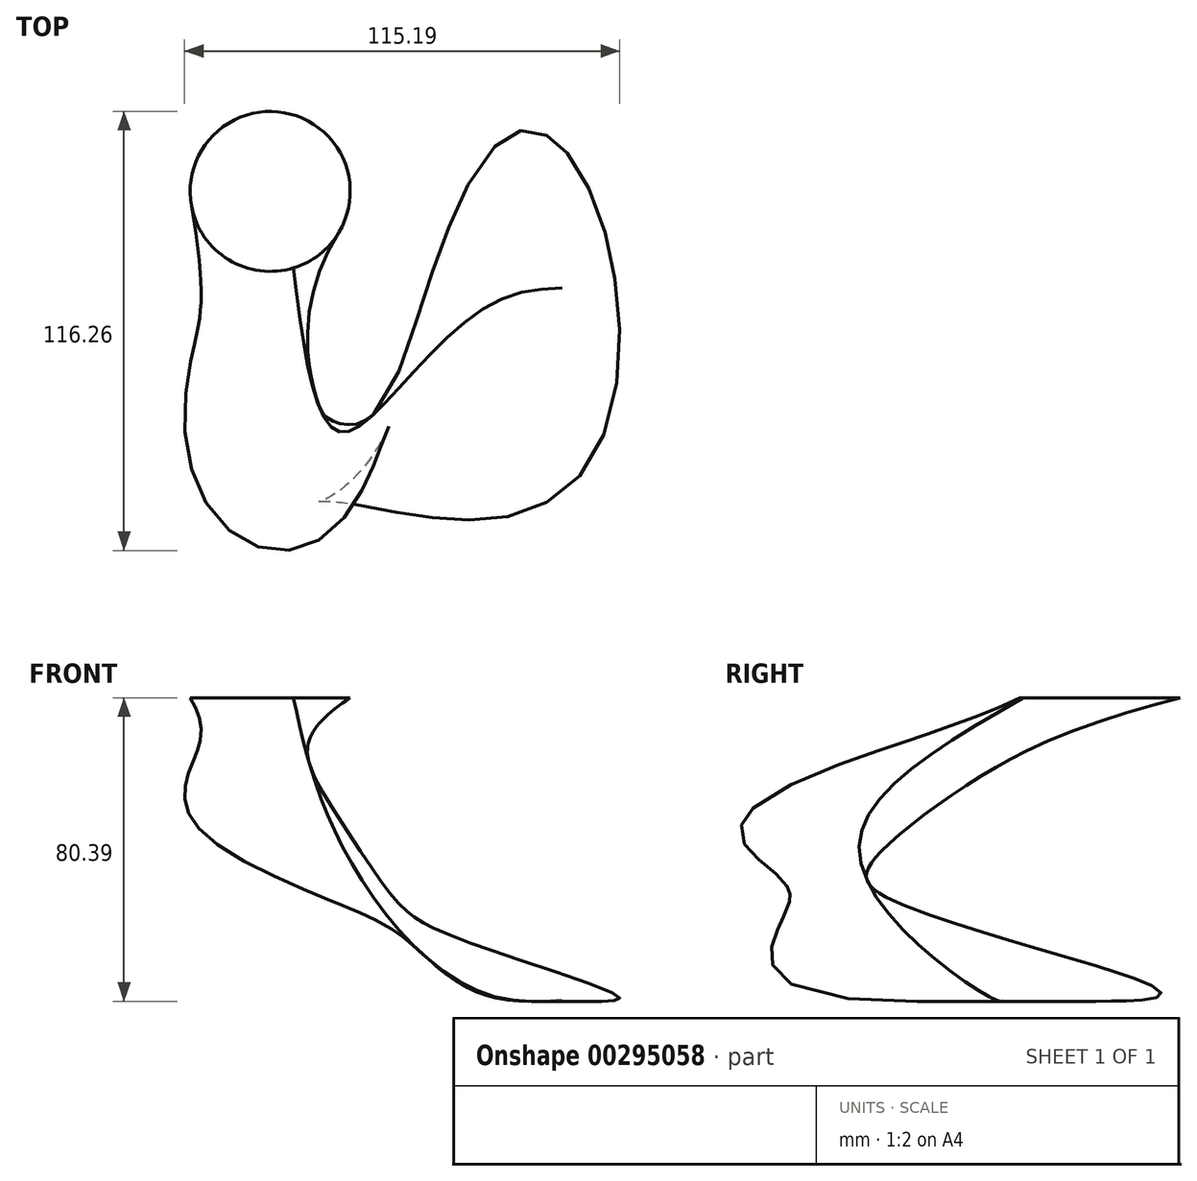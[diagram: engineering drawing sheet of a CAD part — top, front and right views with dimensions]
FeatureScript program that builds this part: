
annotation { "Feature Type Name" : "Feature", "Feature Type Description" : "" }
export const myFeature = defineFeature(function(context is Context, id is Id, definition is map)
    precondition{}
    {
        {
            var Q0;
            Q0=qCreatedBy(makeId("Top.planeOp"),FACE);
            cPlane(context, id + "F0", {"entities" : qUnion([Q0]), "cplaneType" : CPlaneType.OFFSET, "offset" : 40 * mm, "width" : 152.4 * mm, "height" : 152.4 * mm});
        }
        {
            var Q0;
            Q0=qCreatedBy(id+"F0.planeOp",FACE);
            cPlane(context, id + "F1", {"entities" : qUnion([Q0]), "cplaneType" : CPlaneType.OFFSET, "offset" : 40 * mm, "width" : 150 * mm, "height" : 150 * mm});
        }
        {
            var Q0;
            Q0=qCreatedBy(id+"F1.planeOp",FACE);
            var sketch = newSketch(context, id + "F2", { "sketchPlane" : qUnion([Q0])});
            skCircle(sketch, "E0", {"center": v(-32, 25.6) * mm, "radius": 21.18 * mm});
            skSolve(sketch);
        }
        {
            var Q0;
            Q0=qCreatedBy(id+"F0.planeOp",FACE);
            var sketch = newSketch(context, id + "F3", { "sketchPlane" : qUnion([Q0])});
            skCircle(sketch, "E1", {"center": v(-26.42, -49.6) * mm, "radius": 17.98 * mm});
            skPoint(sketch, "E1.first.point", {"position": v(-44.38, -50.45) * mm});
            skPoint(sketch, "E1.second.point", {"position": v(-11.98, -60.29) * mm});
            skPoint(sketch, "E1.third.point", {"position": v(-26.65, -67.57) * mm});
            skSolve(sketch);
        }
        {
            var Q0;
            Q0=qCreatedBy(makeId("Top.planeOp"),FACE);
            var sketch = newSketch(context, id + "F4", { "sketchPlane" : qUnion([Q0])});
            skEllipse(sketch, "E2", {"center": v(45.2, 0) * mm, "majorRadius": 37.38 * mm, "minorRadius": 14.08 * mm, "majorAxis": v(0.15, -0.99)});
            skSolve(sketch);
        }
        {
            var Q0;
            Q0=sQuery(id+"F4.wireOp",VERTEX,"E2.center");
            var Q1;
            Q1=makeQuery(id+"F4.imprint","IMPRINT",FACE,{"disambiguationData":[TD([[makeQuery(id+"F4.imprint","IMPRINT",EDGE,{"derivedFrom":sQuery(id+"F4.wireOp",EDGE,"E2")}),1.0]])]});
            var Q2;
            Q2=makeQuery(id+"F3.imprint","IMPRINT",FACE,{"disambiguationData":[TD([[makeQuery(id+"F3.imprint","IMPRINT",EDGE,{"derivedFrom":sQuery(id+"F3.wireOp",EDGE,"E1")}),1.0]])]});
            var Q3;
            Q3=makeQuery(id+"F2.imprint","IMPRINT",FACE,{"disambiguationData":[TD([[makeQuery(id+"F2.imprint","IMPRINT",EDGE,{"derivedFrom":sQuery(id+"F2.wireOp",EDGE,"E0")}),1.0]])]});
            loft(context, id + "F5", {"sheetProfilesArray" : [{ "sheetProfileEntities" : qUnion([Q0]) }, { "sheetProfileEntities" : qUnion([Q1]) }, { "sheetProfileEntities" : qUnion([Q2]) }, { "sheetProfileEntities" : qUnion([Q3]) }]});
        }
    });
